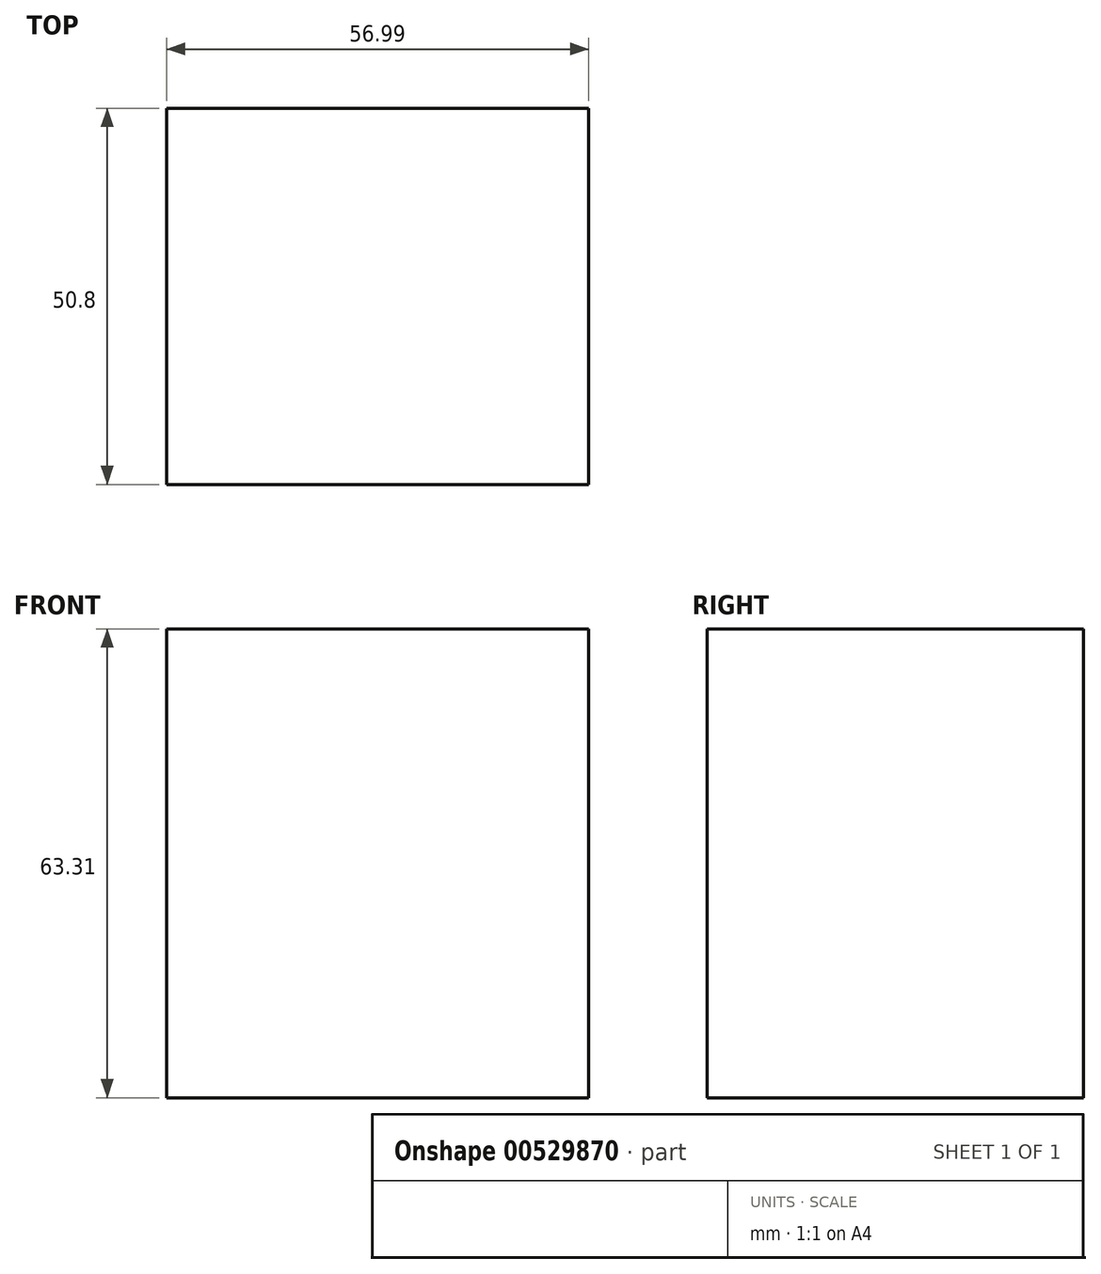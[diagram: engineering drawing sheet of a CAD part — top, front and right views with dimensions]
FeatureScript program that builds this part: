
annotation { "Feature Type Name" : "Feature", "Feature Type Description" : "" }
export const myFeature = defineFeature(function(context is Context, id is Id, definition is map)
    precondition{}
    {
        {
            var Q0;
            Q0=qCreatedBy(makeId("Front.planeOp"),FACE);
            var sketch = newSketch(context, id + "F0", { "sketchPlane" : qUnion([Q0])});
            skLineSegment(sketch, "E0.bottom", {"start": v(-27.35, 17.94) * mm, "end": v(29.64, 17.94) * mm});
            skLineSegment(sketch, "E0.top", {"start": v(-27.35, -19.97) * mm, "end": v(29.64, -19.97) * mm});
            skLineSegment(sketch, "E0.left", {"start": v(-27.35, 17.94) * mm, "end": v(-27.35, -19.97) * mm});
            skLineSegment(sketch, "E0.right", {"start": v(29.64, 17.94) * mm, "end": v(29.64, -19.97) * mm});
            skSolve(sketch);
        }
        {
            var Q0;
            Q0=makeQuery(id+"F0.imprint","IMPRINT",FACE,{"disambiguationData":[TD([[makeQuery(id+"F0.imprint","IMPRINT",EDGE,{"derivedFrom":sQuery(id+"F0.wireOp",EDGE,"E0.bottom")}),-1.0]])]});
            extrude(context, id + "F1", {"entities" : qUnion([Q0]), "depth" : 50.8 * mm, "offsetDistance" : 25.4 * mm});
        }
        {
            var Q0;
            Q0=makeQuery(id+"F1.opExtrude","SWEPT_FACE",FACE,{"disambiguationData":[OSD([sQuery(id+"F0.wireOp",EDGE,"E0.bottom")])]});
            extrude(context, id + "F2", {"entities" : qUnion([Q0]), "operationType" : NewBodyOperationType.ADD, "depth" : 25.4 * mm, "offsetDistance" : 25.4 * mm});
        }
    });
